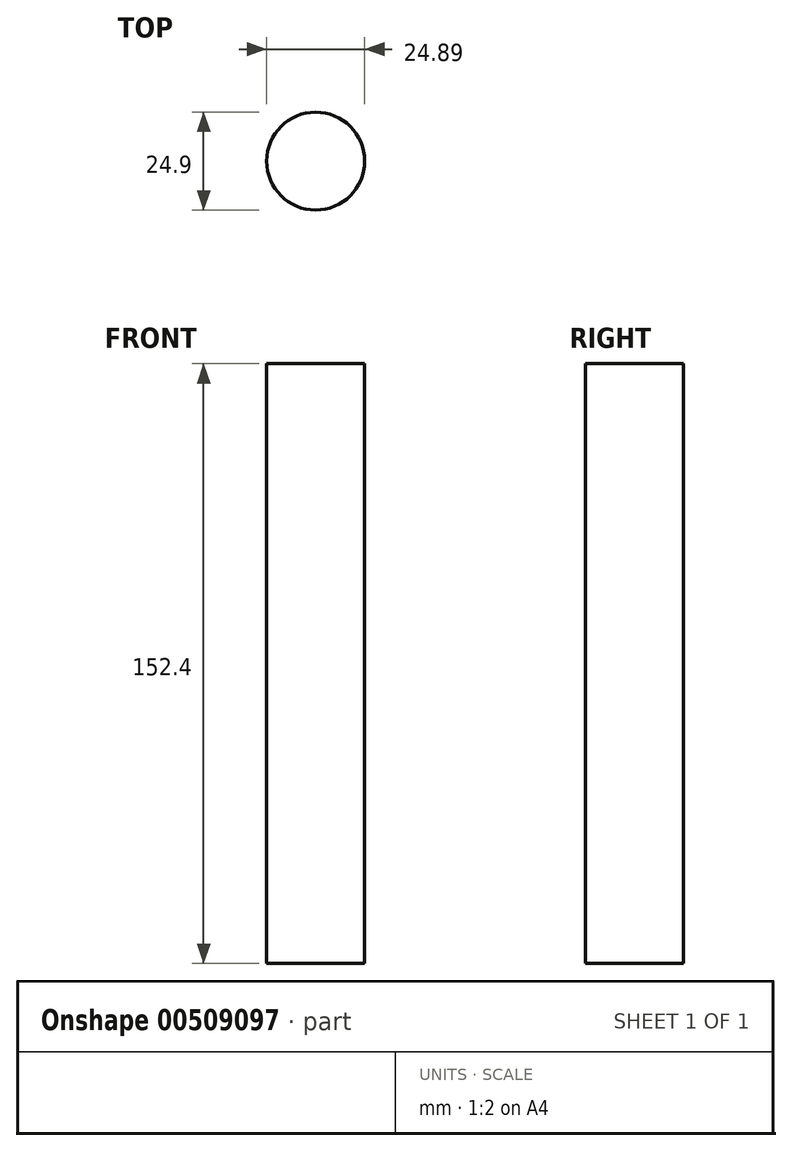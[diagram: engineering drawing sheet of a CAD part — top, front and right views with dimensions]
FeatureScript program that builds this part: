
annotation { "Feature Type Name" : "Feature", "Feature Type Description" : "" }
export const myFeature = defineFeature(function(context is Context, id is Id, definition is map)
    precondition{}
    {
        {
            var Q0;
            Q0=qCreatedBy(makeId("Front.planeOp"),FACE);
            var sketch = newSketch(context, id + "F0", { "sketchPlane" : qUnion([Q0])});
            skLineSegment(sketch, "E0.bottom", {"start": v(42.92, 35.54) * mm, "end": v(55.37, 35.54) * mm});
            skLineSegment(sketch, "E0.top", {"start": v(42.92, 187.94) * mm, "end": v(55.37, 187.94) * mm});
            skLineSegment(sketch, "E0.left", {"start": v(42.92, 35.54) * mm, "end": v(42.92, 187.94) * mm});
            skLineSegment(sketch, "E0.right", {"start": v(55.37, 35.54) * mm, "end": v(55.37, 187.94) * mm});
            skSolve(sketch);
        }
        {
            var Q0;
            Q0=makeQuery(id+"F0.imprint","IMPRINT",FACE,{"disambiguationData":[TD([[makeQuery(id+"F0.imprint","IMPRINT",EDGE,{"derivedFrom":sQuery(id+"F0.wireOp",EDGE,"E0.bottom")}),1.0]])]});
            var Q1;
            Q1=sQuery(id+"F0.wireOp",EDGE,"E0.left");
            revolve(context, id + "F1", {"entities" : qUnion([Q0]), "axis" : qUnion([Q1]), "revolveType" : RevolveType.FULL});
        }
    });
